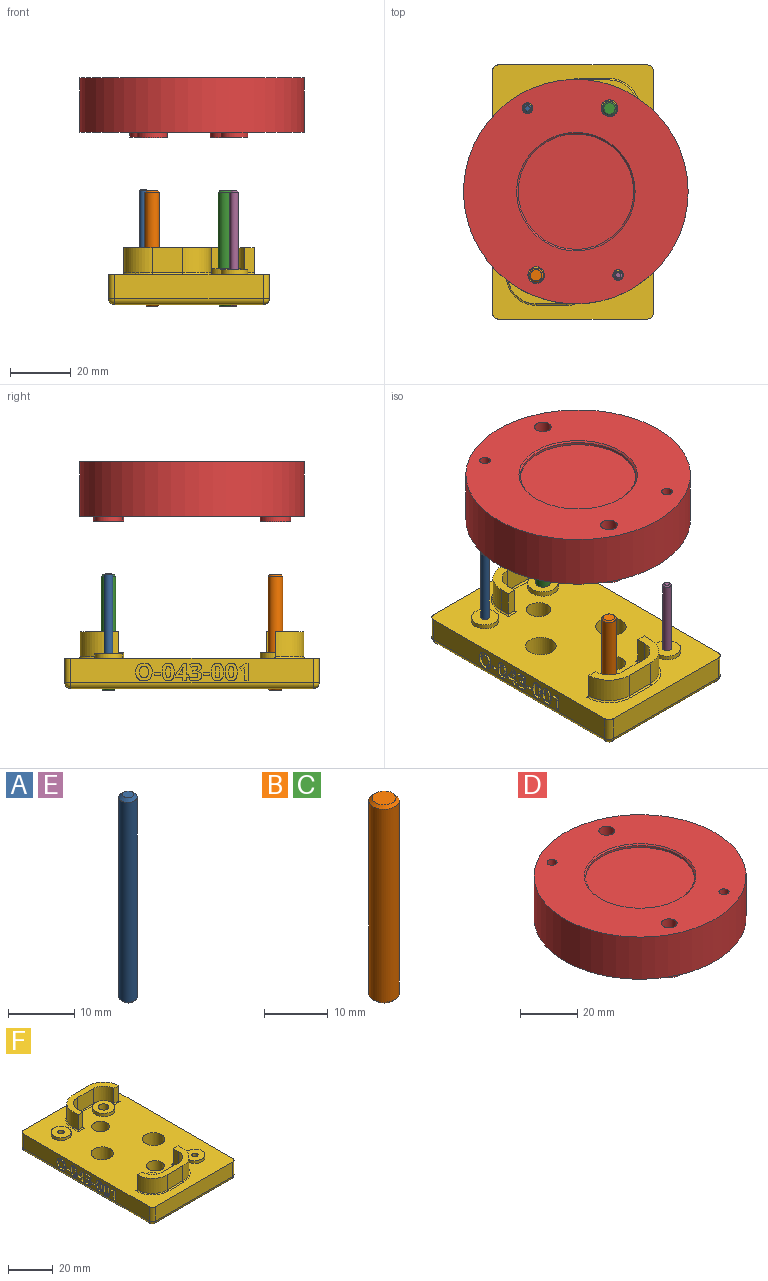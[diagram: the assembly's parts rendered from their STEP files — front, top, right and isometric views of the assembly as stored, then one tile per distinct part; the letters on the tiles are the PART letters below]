
ASSEMBLY  parts=6 mates=5
PART A: 5 faces, bbox 2.8x2.8x38 mm
  f0: cylinder r=1.39mm len=37mm, axis (0,0,-1), area 323.1mm2, adj f3,f4
  f1: plane 1.78x1.78mm, normal (0,0,1), area 2.5mm2, adj f4
  f2: plane 1.78x1.78mm, normal (0,0,-1), area 2.5mm2, adj f3
  f3: cone r=1.39mm half-angle=45deg, axis (0,0,1), area 5.1mm2, adj f0,f2
  f4: cone r=0.89mm half-angle=45deg, axis (0,0,-1), area 5.1mm2, adj f0,f1
PART B: 5 faces, bbox 4.8x4.8x38 mm
  f0: cylinder r=2.38mm len=37mm, axis (0,0,-1), area 553.3mm2, adj f3,f4
  f1: plane 3.76x3.76mm, normal (0,0,1), area 11.1mm2, adj f4
  f2: plane 3.76x3.76mm, normal (0,0,-1), area 11.1mm2, adj f3
  f3: cone r=2.38mm half-angle=45deg, axis (0,0,1), area 9.5mm2, adj f0,f2
  f4: cone r=1.88mm half-angle=45deg, axis (0,0,-1), area 9.5mm2, adj f0,f1
PART C: same geometry as B
PART D: 179 faces, bbox 74x74x19.8 mm
  f0: plane 74x74mm, normal (0,0,-1), area 3673.8mm2, adj f6,f8,f10,f12,f14,f16,f18,f20
  f1: plane 74x74mm, normal (0,0,1), area 3039.5mm2, adj f2,f3,f4,f5,f24,f178
  f2: cylinder r=2.75mm len=19.75mm, axis (0,0,-1), area 341.3mm2, adj f1,f19
  f3: cylinder r=1.75mm len=19.5mm, axis (0,0,-1), area 214.4mm2, adj f1,f17
  f4: cylinder r=2.75mm len=19.75mm, axis (0,0,-1), area 341.3mm2, adj f1,f21
  f5: cylinder r=1.75mm len=19.5mm, axis (0,0,-1), area 214.4mm2, adj f1,f15
  f6: cylinder r=4mm len=8mm, axis (0,0,-1), area 201.1mm2, adj f0,f7
  f7: plane 8x8mm, normal (0,0,-1), area 50.3mm2, adj f6
  f8: cylinder r=5mm len=10mm, axis (0,0,-1), area 251.3mm2, adj f0,f9
  f9: plane 10x10mm, normal (0,0,-1), area 78.5mm2, adj f8
  f10: cylinder r=4mm len=8mm, axis (0,0,-1), area 201.1mm2, adj f0,f11
  f11: plane 8x8mm, normal (0,0,-1), area 50.3mm2, adj f10
  f12: cylinder r=5mm len=10mm, axis (0,0,-1), area 251.3mm2, adj f0,f13
  f13: plane 10x10mm, normal (0,0,-1), area 78.5mm2, adj f12
  f14: cylinder r=4.5mm len=9mm, axis (0,0,1), area 42.4mm2, adj f0,f15
  f15: plane 9x9mm, normal (0,0,-1), area 54mm2, adj f5,f14
  f16: cylinder r=4.5mm len=9mm, axis (0,0,1), area 42.4mm2, adj f0,f17
  f17: plane 9x9mm, normal (0,0,-1), area 54mm2, adj f3,f16
  f18: cylinder r=5mm len=10mm, axis (0,0,1), area 55mm2, adj f0,f19
  f19: plane 10x10mm, normal (0,0,-1), area 54.8mm2, adj f2,f18
  f20: cylinder r=5mm len=10mm, axis (0,0,1), area 55mm2, adj f0,f21
  f21: plane 10x10mm, normal (0,0,-1), area 54.8mm2, adj f4,f20
  f22: cylinder r=19mm len=38mm, axis (0,0,-1), area 95.5mm2, adj f23,f178
  f23: plane 38x38mm, normal (0,0,1), area 1134.1mm2, adj f22
  f24: cylinder r=37mm len=74mm, axis (0,0,1), area 4184.6mm2, adj f0,f1
  f25: plane 1.71x1mm, normal (1,0,0), area 1.7mm2, adj f0,f26,f28,f29
  f26: plane 1x0.8mm, normal (0,-1,0), area 0.8mm2, adj f0,f25,f27,f29
  f27: plane 1.71x1mm, normal (-1,0,0), area 1.7mm2, adj f0,f26,f28,f29
  f28: plane 1x0.8mm, normal (0,1,0), area 0.8mm2, adj f0,f25,f27,f29
  f29: plane 1.71x0.8mm, normal (0,0,-1), area 1.4mm2, adj f25,f26,f27,f28
  f30: extruded ~1.79x1mm, area 1.9mm2, adj f0,f31,f45,f46
  f31: extruded ~1.22x1mm, area 1.4mm2, adj f0,f30,f32,f46
  f32: extruded ~1.23x1mm, area 1.4mm2, adj f0,f31,f33,f46
  f33: extruded ~1.82x1mm, area 1.9mm2, adj f0,f32,f34,f46
  f34: extruded ~1.79x1mm, area 1.9mm2, adj f0,f33,f35,f46
  f35: extruded ~1.22x1mm, area 1.4mm2, adj f0,f34,f36,f46
  f36: extruded ~1.23x1mm, area 1.4mm2, adj f0,f35,f45,f46
  f37: extruded ~1.23x1mm, area 1.2mm2, adj f38,f44,f46,f47
  f38: extruded ~1x0.5mm, area 0.7mm2, adj f37,f39,f46,f47
  f39: extruded ~1x0.5mm, area 0.7mm2, adj f38,f40,f46,f47
  f40: extruded ~1.23x1mm, area 1.2mm2, adj f39,f41,f46,f47
  f41: extruded ~1.22x1mm, area 1.2mm2, adj f40,f42,f46,f47
  f42: extruded ~1x0.5mm, area 0.7mm2, adj f41,f43,f46,f47
  f43: extruded ~1x0.5mm, area 0.7mm2, adj f42,f44,f46,f47
  f44: extruded ~1.23x1mm, area 1.2mm2, adj f37,f43,f46,f47
  f45: extruded ~1.81x1mm, area 1.9mm2, adj f0,f30,f36,f46
  f46: plane 4.8x3.26mm, normal (0,0,-1), area 9.5mm2, adj f30,f31,f32,f33,f34,f35,f36,f37
  f47: plane 3.21x1.3mm, normal (0,0,-1), area 3.5mm2, adj f37,f38,f39,f40,f41,f42,f43,f44
  f48: extruded ~1.79x1mm, area 1.9mm2, adj f0,f49,f63,f64
  f49: extruded ~1.22x1mm, area 1.4mm2, adj f0,f48,f50,f64
  f50: extruded ~1.23x1mm, area 1.4mm2, adj f0,f49,f51,f64
  f51: extruded ~1.82x1mm, area 1.9mm2, adj f0,f50,f52,f64
  f52: extruded ~1.79x1mm, area 1.9mm2, adj f0,f51,f53,f64
  f53: extruded ~1.22x1mm, area 1.4mm2, adj f0,f52,f54,f64
  f54: extruded ~1.23x1mm, area 1.4mm2, adj f0,f53,f63,f64
  f55: extruded ~1.23x1mm, area 1.2mm2, adj f56,f62,f64,f65
  f56: extruded ~1x0.5mm, area 0.7mm2, adj f55,f57,f64,f65
  f57: extruded ~1x0.5mm, area 0.7mm2, adj f56,f58,f64,f65
  f58: extruded ~1.23x1mm, area 1.2mm2, adj f57,f59,f64,f65
  f59: extruded ~1.22x1mm, area 1.2mm2, adj f58,f60,f64,f65
  f60: extruded ~1x0.5mm, area 0.7mm2, adj f59,f61,f64,f65
  f61: extruded ~1x0.5mm, area 0.7mm2, adj f60,f62,f64,f65
  f62: extruded ~1.23x1mm, area 1.2mm2, adj f55,f61,f64,f65
  f63: extruded ~1.81x1mm, area 1.9mm2, adj f0,f48,f54,f64
  f64: plane 4.8x3.26mm, normal (0,0,-1), area 9.5mm2, adj f48,f49,f50,f51,f52,f53,f54,f55
  f65: plane 3.21x1.3mm, normal (0,0,-1), area 3.5mm2, adj f55,f56,f57,f58,f59,f60,f61,f62
  f66: plane 1x0.77mm, normal (0,-1,0), area 0.8mm2, adj f0,f67,f83,f84
  f67: plane 1x0.56mm, normal (-1,0,0), area 0.6mm2, adj f0,f66,f68,f84
  f68: plane 2.93x1mm, normal (0,-1,0), area 2.9mm2, adj f0,f67,f69,f84
  f69: plane 1x0.91mm, normal (-1,0,0), area 0.9mm2, adj f0,f68,f70,f84
  f70: plane 3.01x2.05mm, normal (-0.56,0.83,0), area 3.6mm2, adj f0,f69,f71,f84
  f71: plane 1x0.69mm, normal (0,1,0), area 0.7mm2, adj f0,f70,f72,f84
  f72: plane 1.99x1mm, normal (1,0,0), area 2mm2, adj f0,f71,f73,f84
  f73: plane 1x0.97mm, normal (0,1,0), area 1mm2, adj f0,f72,f74,f84
  f74: plane 1x0.96mm, normal (1,0,0), area 1mm2, adj f0,f73,f75,f84
  f75: plane 1x0.97mm, normal (0,-1,0), area 1mm2, adj f0,f74,f83,f84
  f76: plane 1.12x1mm, normal (-1,0,0), area 1.1mm2, adj f77,f82,f84,f85
  f77: plane 1.29x1mm, normal (0.55,-0.83,0), area 1.6mm2, adj f76,f78,f84,f85
  f78: extruded ~1x0.51mm, area 0.6mm2, adj f77,f79,f84,f85
  f79: plane 1x0.03mm, normal (1,0,0), area 0mm2, adj f78,f80,f84,f85
  f80: extruded ~1x0.44mm, area 0.4mm2, adj f79,f81,f84,f85
  f81: extruded ~1x0.57mm, area 0.6mm2, adj f80,f82,f84,f85
  f82: plane 1x0.79mm, normal (0,1,0), area 0.8mm2, adj f76,f81,f84,f85
  f83: plane 1x0.56mm, normal (1,0,0), area 0.6mm2, adj f0,f66,f75,f84
  f84: plane 4.67x3.52mm, normal (0,0,-1), area 8.2mm2, adj f66,f67,f68,f69,f70,f71,f72,f73
  f85: plane 1.8x1.17mm, normal (0,0,-1), area 1mm2, adj f76,f77,f78,f79,f80,f81,f82
  f86: extruded ~1.79x1mm, area 1.9mm2, adj f0,f87,f101,f102
  f87: extruded ~1.22x1mm, area 1.4mm2, adj f0,f86,f88,f102
  f88: extruded ~1.23x1mm, area 1.4mm2, adj f0,f87,f89,f102
  f89: extruded ~1.82x1mm, area 1.9mm2, adj f0,f88,f90,f102
  f90: extruded ~1.79x1mm, area 1.9mm2, adj f0,f89,f91,f102
  f91: extruded ~1.22x1mm, area 1.4mm2, adj f0,f90,f92,f102
  f92: extruded ~1.23x1mm, area 1.4mm2, adj f0,f91,f101,f102
  f93: extruded ~1.23x1mm, area 1.2mm2, adj f94,f100,f102,f103
  f94: extruded ~1x0.5mm, area 0.7mm2, adj f93,f95,f102,f103
  f95: extruded ~1x0.5mm, area 0.7mm2, adj f94,f96,f102,f103
  f96: extruded ~1.23x1mm, area 1.2mm2, adj f95,f97,f102,f103
  f97: extruded ~1.22x1mm, area 1.2mm2, adj f96,f98,f102,f103
  f98: extruded ~1x0.5mm, area 0.7mm2, adj f97,f99,f102,f103
  f99: extruded ~1x0.5mm, area 0.7mm2, adj f98,f100,f102,f103
  f100: extruded ~1.23x1mm, area 1.2mm2, adj f93,f99,f102,f103
  f101: extruded ~1.81x1mm, area 1.9mm2, adj f0,f86,f92,f102
  f102: plane 4.8x3.26mm, normal (0,0,-1), area 9.5mm2, adj f86,f87,f88,f89,f90,f91,f92,f93
  f103: plane 3.21x1.3mm, normal (0,0,-1), area 3.5mm2, adj f93,f94,f95,f96,f97,f98,f99,f100
  f104: extruded ~1x0.82mm, area 1mm2, adj f0,f105,f130,f131
  f105: extruded ~1.14x1mm, area 1.2mm2, adj f0,f104,f106,f131
  f106: extruded ~1.52x1mm, area 1.6mm2, adj f0,f105,f107,f131
  f107: plane 1x0.68mm, normal (0.56,0.83,0), area 0.8mm2, adj f0,f106,f108,f131
  f108: extruded ~1x0.53mm, area 0.6mm2, adj f0,f107,f109,f131
  f109: extruded ~1x0.47mm, area 0.5mm2, adj f0,f108,f110,f131
  f110: extruded ~1x0.66mm, area 1mm2, adj f0,f109,f111,f131
  f111: extruded ~1x0.49mm, area 0.6mm2, adj f0,f110,f112,f131
  f112: extruded ~1x0.79mm, area 0.8mm2, adj f0,f111,f113,f131
  f113: plane 1x0.36mm, normal (-1,0,0), area 0.4mm2, adj f0,f112,f114,f131
  f114: plane 1x0.76mm, normal (0,1,0), area 0.8mm2, adj f0,f113,f115,f131
  f115: plane 1x0.35mm, normal (1,0,0), area 0.4mm2, adj f0,f114,f116,f131
  f116: extruded ~1x0.86mm, area 0.9mm2, adj f0,f115,f117,f131
  f117: extruded ~1x0.47mm, area 0.6mm2, adj f0,f116,f118,f131
  f118: extruded ~1x0.53mm, area 0.6mm2, adj f0,f117,f119,f131
  f119: extruded ~1x0.72mm, area 0.8mm2, adj f0,f118,f120,f131
  f120: extruded ~1x0.64mm, area 0.7mm2, adj f0,f119,f121,f131
  f121: extruded ~1x0.6mm, area 0.6mm2, adj f0,f120,f122,f131
  f122: plane 1x0.84mm, normal (0,1,0), area 0.8mm2, adj f0,f121,f123,f131
  f123: extruded ~1.35x1mm, area 1.4mm2, adj f0,f122,f124,f131
  f124: extruded ~1.39x1mm, area 1.5mm2, adj f0,f123,f125,f131
  f125: extruded ~1.05x1mm, area 1.2mm2, adj f0,f124,f126,f131
  f126: extruded ~1x0.74mm, area 0.8mm2, adj f0,f125,f127,f131
  f127: extruded ~1x0.86mm, area 0.9mm2, adj f0,f126,f128,f131
  f128: plane 1x0.02mm, normal (0,-1,0), area 0mm2, adj f0,f127,f129,f131
  f129: extruded ~1x0.74mm, area 0.9mm2, adj f0,f128,f130,f131
  f130: extruded ~1x0.74mm, area 0.8mm2, adj f0,f104,f129,f131
  f131: plane 4.8x3.23mm, normal (0,0,-1), area 8.2mm2, adj f104,f105,f106,f107,f108,f109,f110,f111
  f132: plane 1.71x1mm, normal (1,0,0), area 1.7mm2, adj f0,f133,f135,f136
  f133: plane 1x0.8mm, normal (0,-1,0), area 0.8mm2, adj f0,f132,f134,f136
  f134: plane 1.71x1mm, normal (-1,0,0), area 1.7mm2, adj f0,f133,f135,f136
  f135: plane 1x0.8mm, normal (0,1,0), area 0.8mm2, adj f0,f132,f134,f136
  f136: plane 1.71x0.8mm, normal (0,0,-1), area 1.4mm2, adj f132,f133,f134,f135
  f137: plane 1x0.83mm, normal (0,-1,0), area 0.8mm2, adj f0,f138,f160,f161
  f138: plane 2.03x1mm, normal (-1,0,0), area 2mm2, adj f0,f137,f139,f161
  f139: plane 1x0.04mm, normal (0,-1,0), area 0mm2, adj f0,f138,f140,f161
  f140: plane 1x0.6mm, normal (0.73,-0.69,0), area 0.8mm2, adj f0,f139,f141,f161
  f141: extruded ~1x0.85mm, area 1.2mm2, adj f0,f140,f142,f161
  f142: extruded ~1x0.58mm, area 0.7mm2, adj f0,f141,f143,f161
  f143: extruded ~1x0.61mm, area 0.6mm2, adj f0,f142,f144,f161
  f144: extruded ~1x0.66mm, area 0.7mm2, adj f0,f143,f145,f161
  f145: extruded ~1x0.52mm, area 0.7mm2, adj f0,f144,f146,f161
  f146: extruded ~1x0.77mm, area 0.8mm2, adj f0,f145,f147,f161
  f147: extruded ~1x0.6mm, area 0.6mm2, adj f0,f146,f148,f161
  f148: extruded ~1x0.49mm, area 0.5mm2, adj f0,f147,f149,f161
  f149: extruded ~1x0.57mm, area 0.7mm2, adj f0,f148,f150,f161
  f150: plane 1x0.64mm, normal (0.65,0.76,0), area 0.8mm2, adj f0,f149,f151,f161
  f151: extruded ~1x0.53mm, area 0.6mm2, adj f0,f150,f152,f161
  f152: extruded ~1x0.53mm, area 0.5mm2, adj f0,f151,f153,f161
  f153: extruded ~1x0.41mm, area 0.4mm2, adj f0,f152,f154,f161
  f154: extruded ~1x0.42mm, area 0.5mm2, adj f0,f153,f155,f161
  f155: extruded ~1x0.36mm, area 0.4mm2, adj f0,f154,f156,f161
  f156: extruded ~1x0.38mm, area 0.4mm2, adj f0,f155,f157,f161
  f157: extruded ~1x0.74mm, area 1mm2, adj f0,f156,f158,f161
  f158: plane 1.18x1.17mm, normal (-0.7,0.71,0), area 1.7mm2, adj f0,f157,f159,f161
  f159: plane 1x0.69mm, normal (0,1,0), area 0.7mm2, adj f0,f158,f160,f161
  f160: plane 3.26x1mm, normal (1,0,0), area 3.3mm2, adj f0,f137,f159,f161
  f161: plane 4.73x3.27mm, normal (0,0,-1), area 8.1mm2, adj f137,f138,f139,f140,f141,f142,f143,f144
  f162: extruded ~1.78x1mm, area 1.9mm2, adj f0,f163,f175,f176
  f163: extruded ~1.65x1mm, area 1.8mm2, adj f0,f162,f164,f176
  f164: extruded ~1.65x1mm, area 1.8mm2, adj f0,f163,f165,f176
  f165: extruded ~1.78x1mm, area 1.9mm2, adj f0,f164,f166,f176
  f166: extruded ~1.79x1mm, area 1.9mm2, adj f0,f165,f167,f176
  f167: extruded ~1.65x1mm, area 1.8mm2, adj f0,f166,f168,f176
  f168: extruded ~1.65x1mm, area 1.8mm2, adj f0,f167,f175,f176
  f169: extruded ~1.18x1mm, area 1.2mm2, adj f170,f174,f176,f177
  f170: extruded ~1x0.89mm, area 1mm2, adj f169,f171,f176,f177
  f171: extruded ~1.58x1.18mm, area 2.2mm2, adj f170,f172,f176,f177
  f172: extruded ~1.57x1.18mm, area 2.2mm2, adj f171,f173,f176,f177
  f173: extruded ~1x0.89mm, area 1mm2, adj f172,f174,f176,f177
  f174: extruded ~1.18x1mm, area 1.2mm2, adj f169,f173,f176,f177
  f175: extruded ~1.78x1mm, area 1.9mm2, adj f0,f162,f168,f176
  f176: plane 4.8x4.44mm, normal (0,0,-1), area 11.4mm2, adj f162,f163,f164,f165,f166,f167,f168,f169
  f177: plane 3.15x2.37mm, normal (0,0,-1), area 6.2mm2, adj f169,f170,f171,f172,f173,f174
  f178: cone r=19mm half-angle=45deg, axis (0,0,1), area 85.5mm2, adj f1,f22
PART E: same geometry as A
PART F: 215 faces, bbox 53x83.8x18.8 mm
  f0: plane 79.78x8mm, normal (-1,0,0), area 515.5mm2, adj f3,f44,f45,f46,f47,f49,f50,f51
  f1: plane 48.98x8mm, normal (0,-1,0), area 391.9mm2, adj f3,f188,f192,f194
  f2: plane 48.98x8mm, normal (0,1,0), area 391.9mm2, adj f3,f183,f185,f186
  f3: plane 83.78x52.98mm, normal (0,0,1), area 3581.7mm2, adj f0,f1,f2,f6,f7,f10,f11,f13
  f4: plane 79.78x48.98mm, normal (0,0,-1), area 3601.7mm2, adj f5,f6,f7,f8,f9,f10,f11,f12
  f5: cylinder r=1.41mm len=11.5mm, axis (0,0,-1), area 101.5mm2, adj f4,f14
  f6: cylinder r=5mm len=10mm, axis (0,0,-1), area 314.2mm2, adj f3,f4
  f7: cylinder r=4mm len=10mm, axis (0,0,-1), area 251.3mm2, adj f3,f4
  f8: cylinder r=2.4mm len=11.75mm, axis (0,0,-1), area 176.8mm2, adj f4,f19
  f9: cylinder r=1.41mm len=11.5mm, axis (0,0,-1), area 101.5mm2, adj f4,f16
  f10: cylinder r=5mm len=10mm, axis (0,0,-1), area 314.2mm2, adj f3,f4
  f11: cylinder r=4mm len=10mm, axis (0,0,-1), area 251.3mm2, adj f3,f4
  f12: cylinder r=2.4mm len=11.75mm, axis (0,0,-1), area 176.8mm2, adj f4,f21
  f13: cylinder r=4.5mm len=9mm, axis (0,0,-1), area 42.4mm2, adj f3,f14
  f14: plane 9x9mm, normal (0,0,1), area 57.4mm2, adj f5,f13
  f15: cylinder r=4.5mm len=9mm, axis (0,0,-1), area 42.4mm2, adj f3,f16
  f16: plane 9x9mm, normal (0,0,1), area 57.4mm2, adj f9,f15
  f17: plane 79.78x8mm, normal (1,0,0), area 638.2mm2, adj f3,f185,f191,f194
  f18: cylinder r=5mm len=10mm, axis (0,0,-1), area 55mm2, adj f3,f19
  f19: plane 10x10mm, normal (0,0,1), area 60.5mm2, adj f8,f18
  f20: cylinder r=5mm len=10mm, axis (0,0,-1), area 55mm2, adj f3,f21
  f21: plane 10x10mm, normal (0,0,1), area 60.5mm2, adj f12,f20
  f22: plane 8.25x3mm, normal (0,1,0), area 24.7mm2, adj f23,f31,f32,f197
  f23: cylinder r=9.4mm len=9.4mm, axis (0,0,-1), area 121.8mm2, adj f22,f24,f32,f199
  f24: plane 10x8.25mm, normal (0,-1,0), area 82.5mm2, adj f23,f25,f32,f201
  f25: cylinder r=9.4mm len=9.4mm, axis (0,0,-1), area 121.8mm2, adj f24,f26,f32,f203
  f26: plane 8.25x3mm, normal (1,0,0), area 24.7mm2, adj f25,f27,f32,f204
  f27: plane 8.25x3mm, normal (0,1,0), area 24.7mm2, adj f26,f28,f32,f202
  f28: plane 8.25x3mm, normal (-1,0,0), area 24.7mm2, adj f27,f29,f32,f200
  f29: cylinder r=6.4mm len=8.25mm, axis (0,0,-1), area 82.9mm2, adj f28,f30,f32,f198
  f30: plane 10x8.25mm, normal (0,1,0), area 82.5mm2, adj f29,f31,f32,f196
  f31: cylinder r=6.4mm len=8.25mm, axis (0,0,-1), area 82.9mm2, adj f22,f30,f32,f195
  f32: plane 28.8x12.4mm, normal (0,0,1), area 113.5mm2, adj f22,f23,f24,f25,f26,f27,f28,f29
  f33: plane 8.25x3mm, normal (0,-1,0), area 24.7mm2, adj f34,f42,f43,f207
  f34: cylinder r=9.4mm len=9.4mm, axis (0,0,-1), area 121.8mm2, adj f33,f35,f43,f209
  f35: plane 10x8.25mm, normal (0,1,0), area 82.5mm2, adj f34,f36,f43,f211
  f36: cylinder r=9.4mm len=9.4mm, axis (0,0,-1), area 121.8mm2, adj f35,f37,f43,f213
  f37: plane 8.25x3.3mm, normal (-1,0,0), area 27.2mm2, adj f36,f38,f43,f214
  f38: plane 8.25x3mm, normal (0,-1,0), area 24.7mm2, adj f37,f39,f43,f212
  f39: plane 8.25x3.3mm, normal (1,0,0), area 27.2mm2, adj f38,f40,f43,f210
  f40: cylinder r=6.4mm len=8.25mm, axis (0,0,-1), area 82.9mm2, adj f39,f41,f43,f208
  f41: plane 10x8.25mm, normal (0,-1,0), area 82.5mm2, adj f40,f42,f43,f206
  f42: cylinder r=6.4mm len=8.25mm, axis (0,0,-1), area 82.9mm2, adj f33,f41,f43,f205
  f43: plane 28.8x12.7mm, normal (0,0,1), area 114.4mm2, adj f33,f34,f35,f36,f37,f38,f39,f40
  f44: plane 2.09x1mm, normal (0,0,1), area 2.1mm2, adj f0,f45,f47,f48
  f45: plane 1x0.97mm, normal (0,1,0), area 1mm2, adj f0,f44,f46,f48
  f46: plane 2.09x1mm, normal (0,0,-1), area 2.1mm2, adj f0,f45,f47,f48
  f47: plane 1x0.97mm, normal (0,-1,0), area 1mm2, adj f0,f44,f46,f48
  f48: plane 2.09x0.97mm, normal (-1,0,0), area 2mm2, adj f44,f45,f46,f47
  f49: extruded ~2.19x1mm, area 2.3mm2, adj f0,f50,f64,f65
  f50: extruded ~1.49x1mm, area 1.7mm2, adj f0,f49,f51,f65
  f51: extruded ~1.5x1mm, area 1.7mm2, adj f0,f50,f52,f65
  f52: extruded ~2.22x1mm, area 2.3mm2, adj f0,f51,f53,f65
  f53: extruded ~2.18x1mm, area 2.3mm2, adj f0,f52,f54,f65
  f54: extruded ~1.48x1mm, area 1.7mm2, adj f0,f53,f55,f65
  f55: extruded ~1.5x1mm, area 1.7mm2, adj f0,f54,f64,f65
  f56: extruded ~1.5x1mm, area 1.5mm2, adj f57,f63,f65,f66
  f57: extruded ~1x0.61mm, area 0.8mm2, adj f56,f58,f65,f66
  f58: extruded ~1x0.6mm, area 0.8mm2, adj f57,f59,f65,f66
  f59: extruded ~1.5x1mm, area 1.5mm2, adj f58,f60,f65,f66
  f60: extruded ~1.49x1mm, area 1.5mm2, adj f59,f61,f65,f66
  f61: extruded ~1x0.61mm, area 0.8mm2, adj f60,f62,f65,f66
  f62: extruded ~1x0.61mm, area 0.8mm2, adj f61,f63,f65,f66
  f63: extruded ~1.5x1mm, area 1.5mm2, adj f56,f62,f65,f66
  f64: extruded ~2.2x1mm, area 2.3mm2, adj f0,f49,f55,f65
  f65: plane 5.85x3.97mm, normal (-1,0,0), area 14.2mm2, adj f49,f50,f51,f52,f53,f54,f55,f56
  f66: plane 3.91x1.58mm, normal (-1,0,0), area 5.3mm2, adj f56,f57,f58,f59,f60,f61,f62,f63
  f67: extruded ~2.19x1mm, area 2.3mm2, adj f0,f68,f82,f83
  f68: extruded ~1.49x1mm, area 1.7mm2, adj f0,f67,f69,f83
  f69: extruded ~1.5x1mm, area 1.7mm2, adj f0,f68,f70,f83
  f70: extruded ~2.22x1mm, area 2.3mm2, adj f0,f69,f71,f83
  f71: extruded ~2.18x1mm, area 2.3mm2, adj f0,f70,f72,f83
  f72: extruded ~1.48x1mm, area 1.7mm2, adj f0,f71,f73,f83
  f73: extruded ~1.5x1mm, area 1.7mm2, adj f0,f72,f82,f83
  f74: extruded ~1.5x1mm, area 1.5mm2, adj f75,f81,f83,f84
  f75: extruded ~1x0.61mm, area 0.8mm2, adj f74,f76,f83,f84
  f76: extruded ~1x0.6mm, area 0.8mm2, adj f75,f77,f83,f84
  f77: extruded ~1.5x1mm, area 1.5mm2, adj f76,f78,f83,f84
  f78: extruded ~1.49x1mm, area 1.5mm2, adj f77,f79,f83,f84
  f79: extruded ~1x0.61mm, area 0.8mm2, adj f78,f80,f83,f84
  f80: extruded ~1x0.61mm, area 0.8mm2, adj f79,f81,f83,f84
  f81: extruded ~1.5x1mm, area 1.5mm2, adj f74,f80,f83,f84
  f82: extruded ~2.2x1mm, area 2.3mm2, adj f0,f67,f73,f83
  f83: plane 5.85x3.97mm, normal (-1,0,0), area 14.2mm2, adj f67,f68,f69,f70,f71,f72,f73,f74
  f84: plane 3.91x1.58mm, normal (-1,0,0), area 5.3mm2, adj f74,f75,f76,f77,f78,f79,f80,f81
  f85: plane 1x0.93mm, normal (0,1,0), area 0.9mm2, adj f0,f86,f102,f103
  f86: plane 1x0.68mm, normal (0,0,-1), area 0.7mm2, adj f0,f85,f87,f103
  f87: plane 3.57x1mm, normal (0,1,0), area 3.6mm2, adj f0,f86,f88,f103
  f88: plane 1.11x1mm, normal (0,0,-1), area 1.1mm2, adj f0,f87,f89,f103
  f89: plane 3.67x2.49mm, normal (0,-0.83,-0.56), area 4.4mm2, adj f0,f88,f90,f103
  f90: plane 1x0.84mm, normal (0,-1,0), area 0.8mm2, adj f0,f89,f91,f103
  f91: plane 2.43x1mm, normal (0,0,1), area 2.4mm2, adj f0,f90,f92,f103
  f92: plane 1.18x1mm, normal (0,-1,0), area 1.2mm2, adj f0,f91,f93,f103
  f93: plane 1.17x1mm, normal (0,0,1), area 1.2mm2, adj f0,f92,f94,f103
  f94: plane 1.18x1mm, normal (0,1,0), area 1.2mm2, adj f0,f93,f102,f103
  f95: plane 1.37x1mm, normal (0,0,-1), area 1.4mm2, adj f96,f101,f103,f104
  f96: plane 1.58x1.04mm, normal (0,0.83,0.55), area 1.9mm2, adj f95,f97,f103,f104
  f97: extruded ~1x0.62mm, area 0.7mm2, adj f96,f98,f103,f104
  f98: plane 1x0.03mm, normal (0,0,1), area 0mm2, adj f97,f99,f103,f104
  f99: extruded ~1x0.53mm, area 0.5mm2, adj f98,f100,f103,f104
  f100: extruded ~1x0.7mm, area 0.7mm2, adj f99,f101,f103,f104
  f101: plane 1x0.96mm, normal (0,-1,0), area 1mm2, adj f95,f100,f103,f104
  f102: plane 1x0.68mm, normal (0,0,1), area 0.7mm2, adj f0,f85,f94,f103
  f103: plane 5.69x4.29mm, normal (-1,0,0), area 12.2mm2, adj f85,f86,f87,f88,f89,f90,f91,f92
  f104: plane 2.2x1.42mm, normal (-1,0,0), area 1.4mm2, adj f95,f96,f97,f98,f99,f100,f101
  f105: extruded ~2.19x1mm, area 2.3mm2, adj f0,f106,f120,f121
  f106: extruded ~1.49x1mm, area 1.7mm2, adj f0,f105,f107,f121
  f107: extruded ~1.5x1mm, area 1.7mm2, adj f0,f106,f108,f121
  f108: extruded ~2.22x1mm, area 2.3mm2, adj f0,f107,f109,f121
  f109: extruded ~2.18x1mm, area 2.3mm2, adj f0,f108,f110,f121
  f110: extruded ~1.48x1mm, area 1.7mm2, adj f0,f109,f111,f121
  f111: extruded ~1.5x1mm, area 1.7mm2, adj f0,f110,f120,f121
  f112: extruded ~1.5x1mm, area 1.5mm2, adj f113,f119,f121,f122
  f113: extruded ~1x0.61mm, area 0.8mm2, adj f112,f114,f121,f122
  f114: extruded ~1x0.6mm, area 0.8mm2, adj f113,f115,f121,f122
  f115: extruded ~1.5x1mm, area 1.5mm2, adj f114,f116,f121,f122
  f116: extruded ~1.49x1mm, area 1.5mm2, adj f115,f117,f121,f122
  f117: extruded ~1x0.61mm, area 0.8mm2, adj f116,f118,f121,f122
  f118: extruded ~1x0.61mm, area 0.8mm2, adj f117,f119,f121,f122
  f119: extruded ~1.5x1mm, area 1.5mm2, adj f112,f118,f121,f122
  f120: extruded ~2.2x1mm, area 2.3mm2, adj f0,f105,f111,f121
  f121: plane 5.85x3.97mm, normal (-1,0,0), area 14.2mm2, adj f105,f106,f107,f108,f109,f110,f111,f112
  f122: plane 3.91x1.58mm, normal (-1,0,0), area 5.3mm2, adj f112,f113,f114,f115,f116,f117,f118,f119
  f123: extruded ~1x1mm, area 1.2mm2, adj f0,f124,f149,f150
  f124: extruded ~1.39x1mm, area 1.5mm2, adj f0,f123,f125,f150
  f125: extruded ~1.86x1mm, area 2mm2, adj f0,f124,f126,f150
  f126: plane 1x0.83mm, normal (0,-0.83,0.56), area 1mm2, adj f0,f125,f127,f150
  f127: extruded ~1x0.64mm, area 0.7mm2, adj f0,f126,f128,f150
  f128: extruded ~1x0.57mm, area 0.6mm2, adj f0,f127,f129,f150
  f129: extruded ~1x0.81mm, area 1.2mm2, adj f0,f128,f130,f150
  f130: extruded ~1x0.59mm, area 0.7mm2, adj f0,f129,f131,f150
  f131: extruded ~1x0.97mm, area 1mm2, adj f0,f130,f132,f150
  f132: plane 1x0.44mm, normal (0,0,-1), area 0.4mm2, adj f0,f131,f133,f150
  f133: plane 1x0.92mm, normal (0,-1,0), area 0.9mm2, adj f0,f132,f134,f150
  f134: plane 1x0.43mm, normal (0,0,1), area 0.4mm2, adj f0,f133,f135,f150
  f135: extruded ~1.04x1mm, area 1.1mm2, adj f0,f134,f136,f150
  f136: extruded ~1x0.57mm, area 0.7mm2, adj f0,f135,f137,f150
  f137: extruded ~1x0.65mm, area 0.7mm2, adj f0,f136,f138,f150
  f138: extruded ~1x0.88mm, area 0.9mm2, adj f0,f137,f139,f150
  f139: extruded ~1x0.79mm, area 0.8mm2, adj f0,f138,f140,f150
  f140: extruded ~1x0.73mm, area 0.8mm2, adj f0,f139,f141,f150
  f141: plane 1.02x1mm, normal (0,-1,0), area 1mm2, adj f0,f140,f142,f150
  f142: extruded ~1.64x1mm, area 1.7mm2, adj f0,f141,f143,f150
  f143: extruded ~1.7x1mm, area 1.8mm2, adj f0,f142,f144,f150
  f144: extruded ~1.28x1mm, area 1.5mm2, adj f0,f143,f145,f150
  f145: extruded ~1x0.9mm, area 1mm2, adj f0,f144,f146,f150
  f146: extruded ~1.04x1mm, area 1.1mm2, adj f0,f145,f147,f150
  f147: plane 1x0.02mm, normal (0,1,0), area 0mm2, adj f0,f146,f148,f150
  f148: extruded ~1x0.91mm, area 1.1mm2, adj f0,f147,f149,f150
  f149: extruded ~1x0.91mm, area 1mm2, adj f0,f123,f148,f150
  f150: plane 5.85x3.94mm, normal (-1,0,0), area 12.2mm2, adj f123,f124,f125,f126,f127,f128,f129,f130
  f151: plane 2.09x1mm, normal (0,0,1), area 2.1mm2, adj f0,f152,f154,f155
  f152: plane 1x0.97mm, normal (0,1,0), area 1mm2, adj f0,f151,f153,f155
  f153: plane 2.09x1mm, normal (0,0,-1), area 2.1mm2, adj f0,f152,f154,f155
  f154: plane 1x0.97mm, normal (0,-1,0), area 1mm2, adj f0,f151,f153,f155
  f155: plane 2.09x0.97mm, normal (-1,0,0), area 2mm2, adj f151,f152,f153,f154
  f156: plane 5.69x1mm, normal (0,1,0), area 5.7mm2, adj f0,f157,f165,f166
  f157: plane 1x0.99mm, normal (0,0,-1), area 1mm2, adj f0,f156,f158,f166
  f158: plane 1.83x1.46mm, normal (0,-0.62,-0.78), area 2.3mm2, adj f0,f157,f159,f166
  f159: plane 1x0.72mm, normal (0,-0.78,0.63), area 0.9mm2, adj f0,f158,f160,f166
  f160: plane 1x0.65mm, normal (0,0.63,0.78), area 0.8mm2, adj f0,f159,f161,f166
  f161: extruded ~1x0.42mm, area 0.6mm2, adj f0,f160,f162,f166
  f162: plane 1x0.59mm, normal (0,-1,-0.03), area 0.6mm2, adj f0,f161,f163,f166
  f163: plane 1x0.54mm, normal (0,-1,-0.02), area 0.5mm2, adj f0,f162,f164,f166
  f164: plane 3.29x1mm, normal (0,-1,0), area 3.3mm2, adj f0,f163,f165,f166
  f165: plane 1.2x1mm, normal (0,0,1), area 1.2mm2, adj f0,f156,f164,f166
  f166: plane 5.69x2.82mm, normal (-1,0,0), area 8.4mm2, adj f156,f157,f158,f159,f160,f161,f162,f163
  f167: extruded ~2.17x1mm, area 2.3mm2, adj f0,f168,f180,f181
  f168: extruded ~2x1mm, area 2.2mm2, adj f0,f167,f169,f181
  f169: extruded ~2.01x1mm, area 2.2mm2, adj f0,f168,f170,f181
  f170: extruded ~2.17x1mm, area 2.3mm2, adj f0,f169,f171,f181
  f171: extruded ~2.18x1mm, area 2.3mm2, adj f0,f170,f172,f181
  f172: extruded ~2.01x1mm, area 2.2mm2, adj f0,f171,f173,f181
  f173: extruded ~2.01x1mm, area 2.2mm2, adj f0,f172,f180,f181
  f174: extruded ~1.44x1mm, area 1.5mm2, adj f175,f179,f181,f182
  f175: extruded ~1.08x1mm, area 1.2mm2, adj f174,f176,f181,f182
  f176: extruded ~1.92x1.44mm, area 2.7mm2, adj f175,f177,f181,f182
  f177: extruded ~1.92x1.44mm, area 2.7mm2, adj f176,f178,f181,f182
  f178: extruded ~1.08x1mm, area 1.2mm2, adj f177,f179,f181,f182
  f179: extruded ~1.44x1mm, area 1.5mm2, adj f174,f178,f181,f182
  f180: extruded ~2.17x1mm, area 2.3mm2, adj f0,f167,f173,f181
  f181: plane 5.85x5.41mm, normal (-1,0,0), area 16.9mm2, adj f167,f168,f169,f170,f171,f172,f173,f174
  f182: plane 3.84x2.88mm, normal (-1,0,0), area 9.2mm2, adj f174,f175,f176,f177,f178,f179
  f183: cylinder r=2mm len=8mm, axis (0,0,-1), area 25.1mm2, adj f0,f2,f3,f184
  f184: sphere r=2mm, area 6.3mm2, adj f183,f186,f187
  f185: cylinder r=2mm len=8mm, axis (0,0,-1), area 25.1mm2, adj f2,f3,f17,f189
  f186: cylinder r=2mm len=48.98mm, axis (-1,0,0), area 153.9mm2, adj f2,f4,f184,f189
  f187: cylinder r=2mm len=79.78mm, axis (0,-1,0), area 250.6mm2, adj f0,f4,f184,f190
  f188: cylinder r=2mm len=8mm, axis (0,0,1), area 25.1mm2, adj f0,f1,f3,f190
  f189: sphere r=2mm, area 6.3mm2, adj f185,f186,f191
  f190: sphere r=2mm, area 6.3mm2, adj f187,f188,f192
  f191: cylinder r=2mm len=79.78mm, axis (0,-1,0), area 250.6mm2, adj f4,f17,f189,f193
  f192: cylinder r=2mm len=48.98mm, axis (1,0,0), area 153.9mm2, adj f1,f4,f190,f193
  f193: sphere r=2mm, area 6.3mm2, adj f191,f192,f194
  f194: cylinder r=2mm len=8mm, axis (0,0,1), area 25.1mm2, adj f1,f3,f17,f193
  f195: torus R=5.9mm, axis (0,0,1), area 7.8mm2, adj f3,f31,f196,f197
  f196: cylinder r=0.5mm len=10mm, axis (1,0,0), area 7.9mm2, adj f3,f30,f195,f198
  f197: cylinder r=0.5mm len=4.01mm, axis (1,0,0), area 2.6mm2, adj f3,f22,f195,f199
  f198: torus R=5.9mm, axis (0,0,1), area 7.7mm2, adj f3,f29,f196,f200
  f199: torus R=9.9mm, axis (0,0,1), area 12mm2, adj f3,f23,f197,f201
  f200: cylinder r=0.5mm len=3.5mm, axis (0,1,0), area 2.5mm2, adj f3,f28,f198,f202
  f201: cylinder r=0.5mm len=10mm, axis (-1,0,0), area 7.9mm2, adj f3,f24,f199,f203
  f202: cylinder r=0.5mm len=4mm, axis (1,0,0), area 2.6mm2, adj f3,f27,f200,f204
  f203: torus R=9.9mm, axis (0,0,1), area 11.8mm2, adj f3,f25,f201,f204
  f204: cylinder r=0.5mm len=3.5mm, axis (0,-1,0), area 2.5mm2, adj f3,f26,f202,f203
  f205: torus R=5.9mm, axis (0,0,1), area 7.8mm2, adj f3,f42,f206,f207
  f206: cylinder r=0.5mm len=10mm, axis (-1,0,0), area 7.9mm2, adj f3,f41,f205,f208
  f207: cylinder r=0.5mm len=4.01mm, axis (-1,0,0), area 2.6mm2, adj f3,f33,f205,f209
  f208: torus R=5.9mm, axis (0,0,1), area 7.7mm2, adj f3,f40,f206,f210
  f209: torus R=9.9mm, axis (0,0,1), area 12mm2, adj f3,f34,f207,f211
  f210: cylinder r=0.5mm len=3.8mm, axis (0,-1,0), area 2.7mm2, adj f3,f39,f208,f212
  f211: cylinder r=0.5mm len=10mm, axis (1,0,0), area 7.9mm2, adj f3,f35,f209,f213
  f212: cylinder r=0.5mm len=4mm, axis (-1,0,0), area 2.6mm2, adj f3,f38,f210,f214
  f213: torus R=9.9mm, axis (0,0,1), area 11.8mm2, adj f3,f36,f211,f214
  f214: cylinder r=0.5mm len=3.8mm, axis (0,1,0), area 2.7mm2, adj f3,f37,f212,f213
PLACE A rot(axis=(0,0,1),90deg) t=(-86.51,-21.28,29.69)mm
PLACE B rot(axis=(0,0,1),90deg) t=(-83.66,-98.28,29.19)mm
PLACE C rot(axis=(0,0,1),90deg) t=(-59.51,-43.3,29.19)mm
PLACE D t=(-48.66,-95.75,86.42)mm
PLACE E rot(axis=(0,0,1),90deg) t=(-56.66,-76.25,29.19)mm
PLACE F t=(-45.08,-95.75,29.69)mm
MATE fastened B.f0 <-> F.f8  axis (0,0,1) through (-83.66,-88.75,29.69)mm
MATE slider D.f4 <-> C.f0  axis (0,0,-1) through (-59.51,-33.78,84.67)mm
MATE fastened C.f0 <-> F.f12  axis (0,0,1) through (-59.51,-33.78,29.69)mm
MATE fastened A.f0 <-> F.f5  axis (0,0,-1) through (-86.51,-33.78,29.69)mm
MATE fastened E.f0 <-> F.f9  axis (0,0,1) through (-56.66,-88.75,29.69)mm
